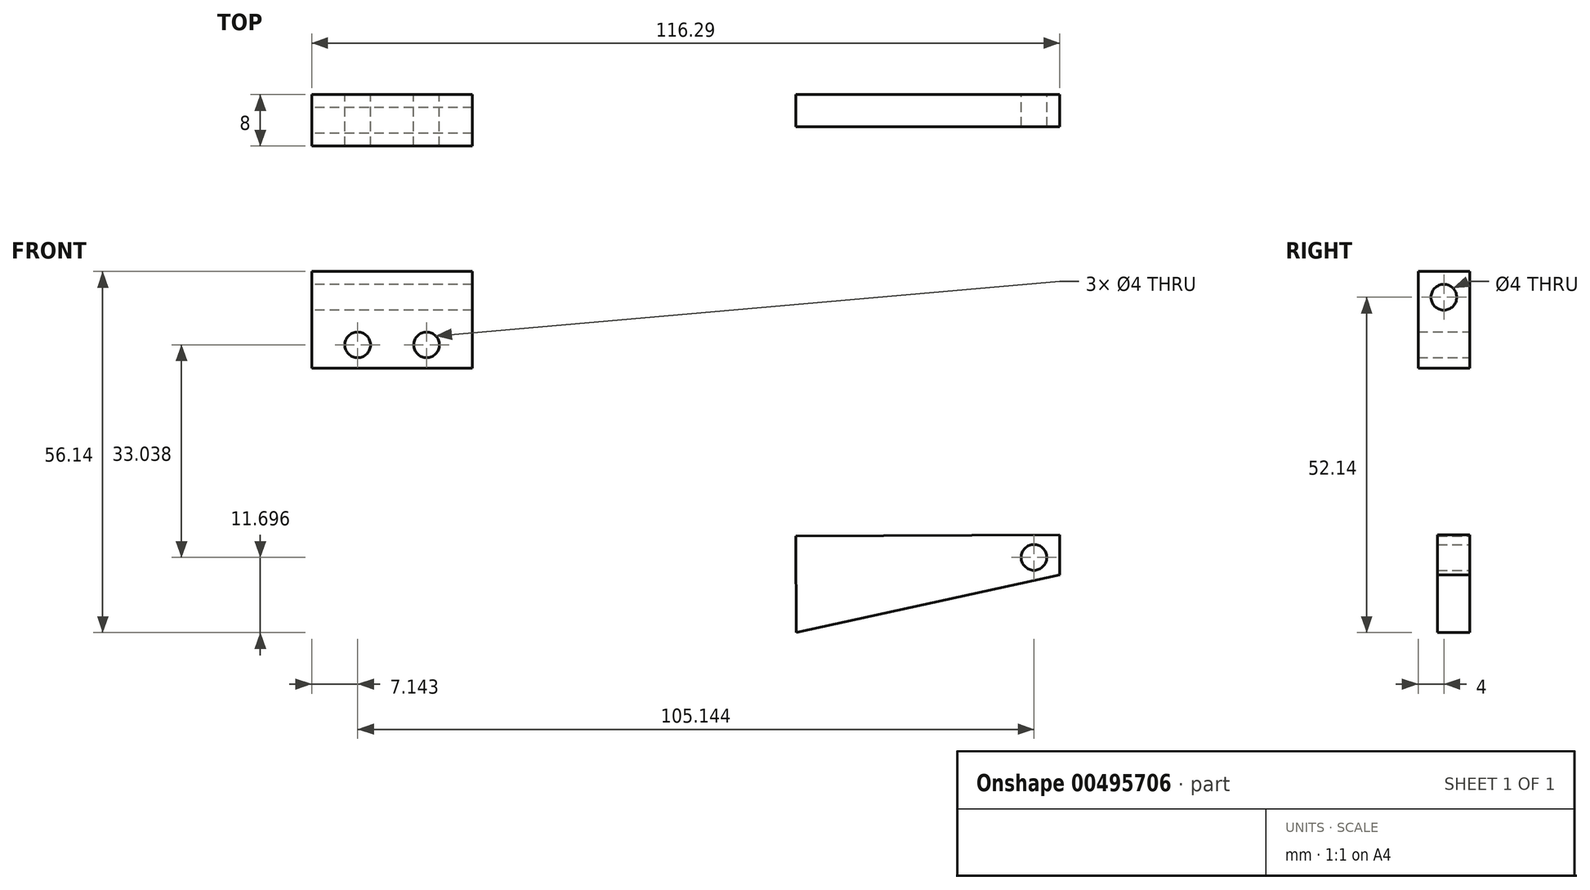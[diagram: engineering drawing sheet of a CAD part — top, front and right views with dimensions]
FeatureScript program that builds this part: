
annotation { "Feature Type Name" : "Feature", "Feature Type Description" : "" }
export const myFeature = defineFeature(function(context is Context, id is Id, definition is map)
    precondition{}
    {
        {
            var Q0;
            Q0=qCreatedBy(makeId("Front.planeOp"),FACE);
            var sketch = newSketch(context, id + "F0", { "sketchPlane" : qUnion([Q0])});
            skLineSegment(sketch, "E0.0", {"start": v(-4.37, 7.48) * mm, "end": v(36.65, 7.7) * mm});
            skLineSegment(sketch, "E0.1", {"start": v(36.65, 1.48) * mm, "end": v(-4.29, -7.52) * mm});
            skLineSegment(sketch, "E0.2", {"start": v(-4.29, -7.52) * mm, "end": v(-4.37, 7.48) * mm});
            skPoint(sketch, "E0.0.midPoint", {"position": v(30.63, 7.67) * mm});
            skCircle(sketch, "E1", {"center": v(32.65, 4.18) * mm, "radius": 2 * mm});
            skLineSegment(sketch, "E2", {"start": v(36.65, 7.7) * mm, "end": v(36.65, 1.48) * mm});
            skPoint(sketch, "E3.orphan", {"position": v(65.63, 7.85) * mm});
            skSolve(sketch);
        }
        {
            var Q0;
            Q0=makeQuery(id+"F0.imprint","IMPRINT",FACE,{"disambiguationData":[TD([[makeQuery(id+"F0.imprint","IMPRINT",EDGE,{"derivedFrom":sQuery(id+"F0.wireOp",EDGE,"E0.0")}),-1.0]])]});
            extrude(context, id + "F1", {"entities" : qUnion([Q0]), "depth" : 5 * mm});
        }
        {
            var Q0;
            Q0=qCreatedBy(makeId("Front.planeOp"),FACE);
            var sketch = newSketch(context, id + "F2", { "sketchPlane" : qUnion([Q0])});
            skLineSegment(sketch, "E4.bottom", {"start": v(-79.64, 33.62) * mm, "end": v(-54.64, 33.62) * mm});
            skLineSegment(sketch, "E4.top", {"start": v(-79.64, 48.62) * mm, "end": v(-54.64, 48.62) * mm});
            skLineSegment(sketch, "E4.left", {"start": v(-79.64, 33.62) * mm, "end": v(-79.64, 48.62) * mm});
            skLineSegment(sketch, "E4.right", {"start": v(-54.64, 33.62) * mm, "end": v(-54.64, 48.62) * mm});
            skCircle(sketch, "E5", {"center": v(-72.5, 37.21) * mm, "radius": 2 * mm});
            skCircle(sketch, "E6", {"center": v(-61.8, 37.21) * mm, "radius": 2 * mm});
            skSolve(sketch);
        }
        {
            var Q0;
            Q0=makeQuery(id+"F2.imprint","IMPRINT",FACE,{"disambiguationData":[TD([[makeQuery(id+"F2.imprint","IMPRINT",EDGE,{"derivedFrom":sQuery(id+"F2.wireOp",EDGE,"E4.bottom")}),1.0]])]});
            extrude(context, id + "F3", {"entities" : qUnion([Q0]), "depth" : 8 * mm});
        }
        {
            var Q0;
            Q0=makeQuery(id+"F3.opExtrude","SWEPT_FACE",FACE,{"disambiguationData":[OSD([sQuery(id+"F2.wireOp",EDGE,"E4.left")])]});
            var sketch = newSketch(context, id + "F4", { "sketchPlane" : qUnion([Q0])});
            skCircle(sketch, "E7", {"center": v(4, 44.62) * mm, "radius": 2 * mm});
            skSolve(sketch);
        }
        {
            var Q0;
            Q0=makeQuery(id+"F4.imprint","IMPRINT",FACE,{"disambiguationData":[TD([[makeQuery(id+"F4.imprint","IMPRINT",EDGE,{"derivedFrom":sQuery(id+"F4.wireOp",EDGE,"E7")}),1.0]])]});
            extrude(context, id + "F5", {"entities" : qUnion([Q0]), "operationType" : NewBodyOperationType.REMOVE, "oppositeDirection" : true, "depth" : 25 * mm});
        }
    });
